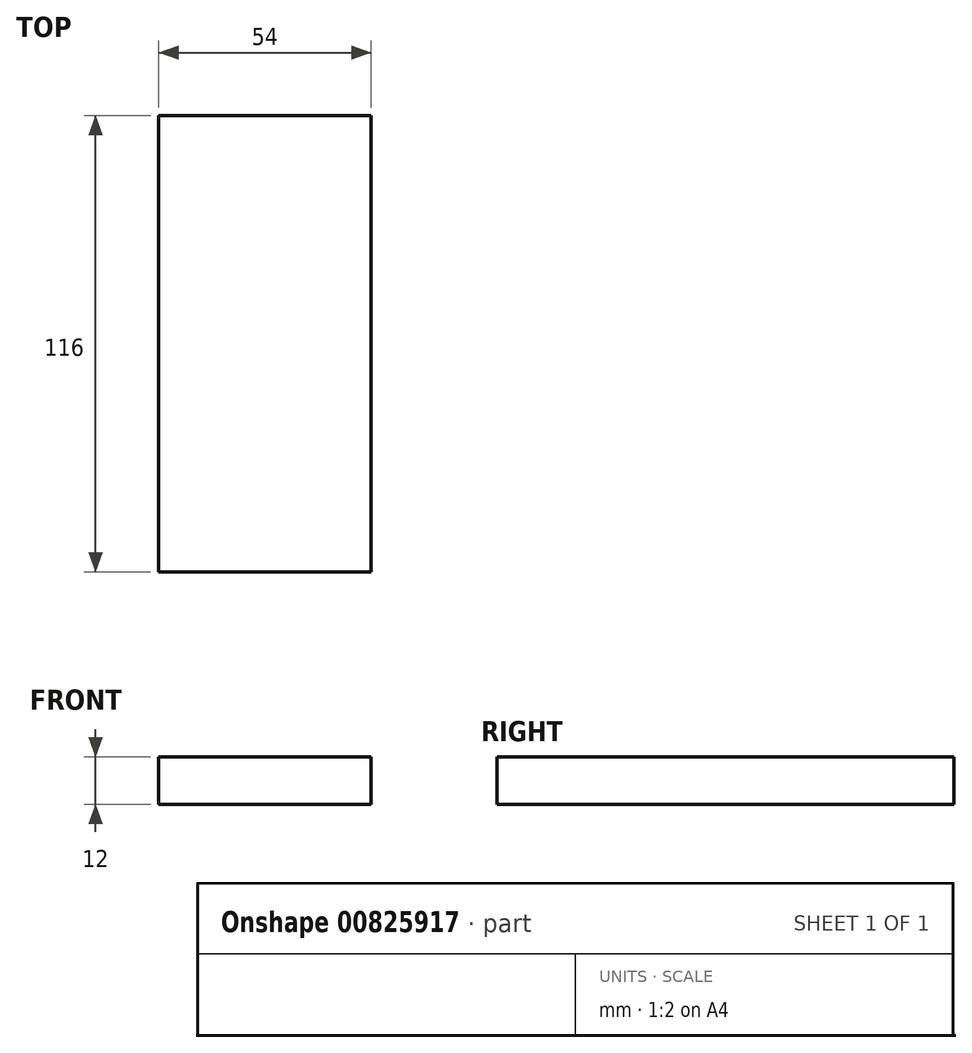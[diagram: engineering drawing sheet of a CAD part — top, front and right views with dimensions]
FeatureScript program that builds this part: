
annotation { "Feature Type Name" : "Feature", "Feature Type Description" : "" }
export const myFeature = defineFeature(function(context is Context, id is Id, definition is map)
    precondition{}
    {
        {
            var Q0;
            Q0=qCreatedBy(makeId("Front.planeOp"),FACE);
            var sketch = newSketch(context, id + "F0", { "sketchPlane" : qUnion([Q0])});
            skLineSegment(sketch, "E0.bottom", {"start": v(27, 6) * mm, "end": v(-27, 6) * mm});
            skLineSegment(sketch, "E0.top", {"start": v(27, -6) * mm, "end": v(-27, -6) * mm});
            skLineSegment(sketch, "E0.left", {"start": v(27, 6) * mm, "end": v(27, -6) * mm});
            skLineSegment(sketch, "E0.right", {"start": v(-27, 6) * mm, "end": v(-27, -6) * mm});
            skPoint(sketch, "E0.middle", {"position": v(0, 0) * mm});
            skSolve(sketch);
        }
        {
            var Q0;
            Q0 = qSketchRegion(id + "F0", true);
            extrude(context, id + "F1", {"entities" : qUnion([Q0]), "endBound" : BoundingType.SYMMETRIC, "depth" : 140 * mm, "offsetDistance" : 25 * mm});
        }
        {
            var Q0;
            Q0=makeQuery(id+"F1.opExtrude","SWEPT_FACE",FACE,{"disambiguationData":[OSD([sQuery(id+"F0.wireOp",EDGE,"E0.bottom")])]});
            var sketch = newSketch(context, id + "F2", { "sketchPlane" : qUnion([Q0])});
            skLineSegment(sketch, "E1.bottom", {"start": v(27, 58) * mm, "end": v(-27, 58) * mm});
            skLineSegment(sketch, "E1.top", {"start": v(27, 70) * mm, "end": v(-27, 70) * mm});
            skLineSegment(sketch, "E1.left", {"start": v(27, 58) * mm, "end": v(27, 70) * mm});
            skLineSegment(sketch, "E1.right", {"start": v(-27, 58) * mm, "end": v(-27, 70) * mm});
            skLineSegment(sketch, "E2.bottom", {"start": v(27, -58) * mm, "end": v(-27, -58) * mm});
            skLineSegment(sketch, "E2.top", {"start": v(27, -70) * mm, "end": v(-27, -70) * mm});
            skLineSegment(sketch, "E2.left", {"start": v(27, -58) * mm, "end": v(27, -70) * mm});
            skLineSegment(sketch, "E2.right", {"start": v(-27, -58) * mm, "end": v(-27, -70) * mm});
            skSolve(sketch);
        }
        {
            var Q0;
            Q0=makeQuery(id+"F2.imprint","IMPRINT",FACE,{"disambiguationData":[TD([[makeQuery(id+"F2.imprint","IMPRINT",EDGE,{"derivedFrom":sQuery(id+"F2.wireOp",EDGE,"E1.bottom")}),-1.0]])]});
            var Q1;
            Q1=makeQuery(id+"F2.imprint","IMPRINT",FACE,{"disambiguationData":[TD([[makeQuery(id+"F2.imprint","IMPRINT",EDGE,{"derivedFrom":sQuery(id+"F2.wireOp",EDGE,"E2.bottom")}),1.0]])]});
            extrude(context, id + "F3", {"entities" : qUnion([Q0, Q1]), "operationType" : NewBodyOperationType.REMOVE, "oppositeDirection" : true, "depth" : 100 * mm, "offsetDistance" : 25 * mm});
        }
    });
